# Revit family: Robe_Hook-Grohe-ATRIO-40312_Series
name_source: partatom
category: Specialty Equipment
revit_build: Autodesk Revit 2014 (Build: 20130308_1515(x64)
units: mm (PartAtom-declared; Revit-internal decimal feet)

## types (2) — shared parameters
Assembly Code = C1030200
Default Elevation = 40"
Description = Atrio Robe Hook
Height = 3 5/8"
Installation Type = Wall Mounted
Length = 3"
Manufacturer = Grohe
Price = Prices may vary. Please consult Manufacturer Representative for most up-to-date price list.
Product Page URL = https://www.grohe.us
URL = https://www.grohe.us
Warranty Documentation Link = https://cdn.cloud.grohe.com
Width = 1 3/8"
cUPC Compliant = Yes

## per-type parameters (varying)
| type | Finish | Material | Model |
| 40312003 | Metal-Grohe-Chrome | Metal-Grohe-Chrome | 40312003 |
| 40312EN3 | Metal-Grohe-Brushed Nickel | Metal-Grohe-Brushed Nickel | 40313EN3 |

## geometry (parser evidence)
native form markers: Sweep x4
no freeform markers — native parametric forms only
